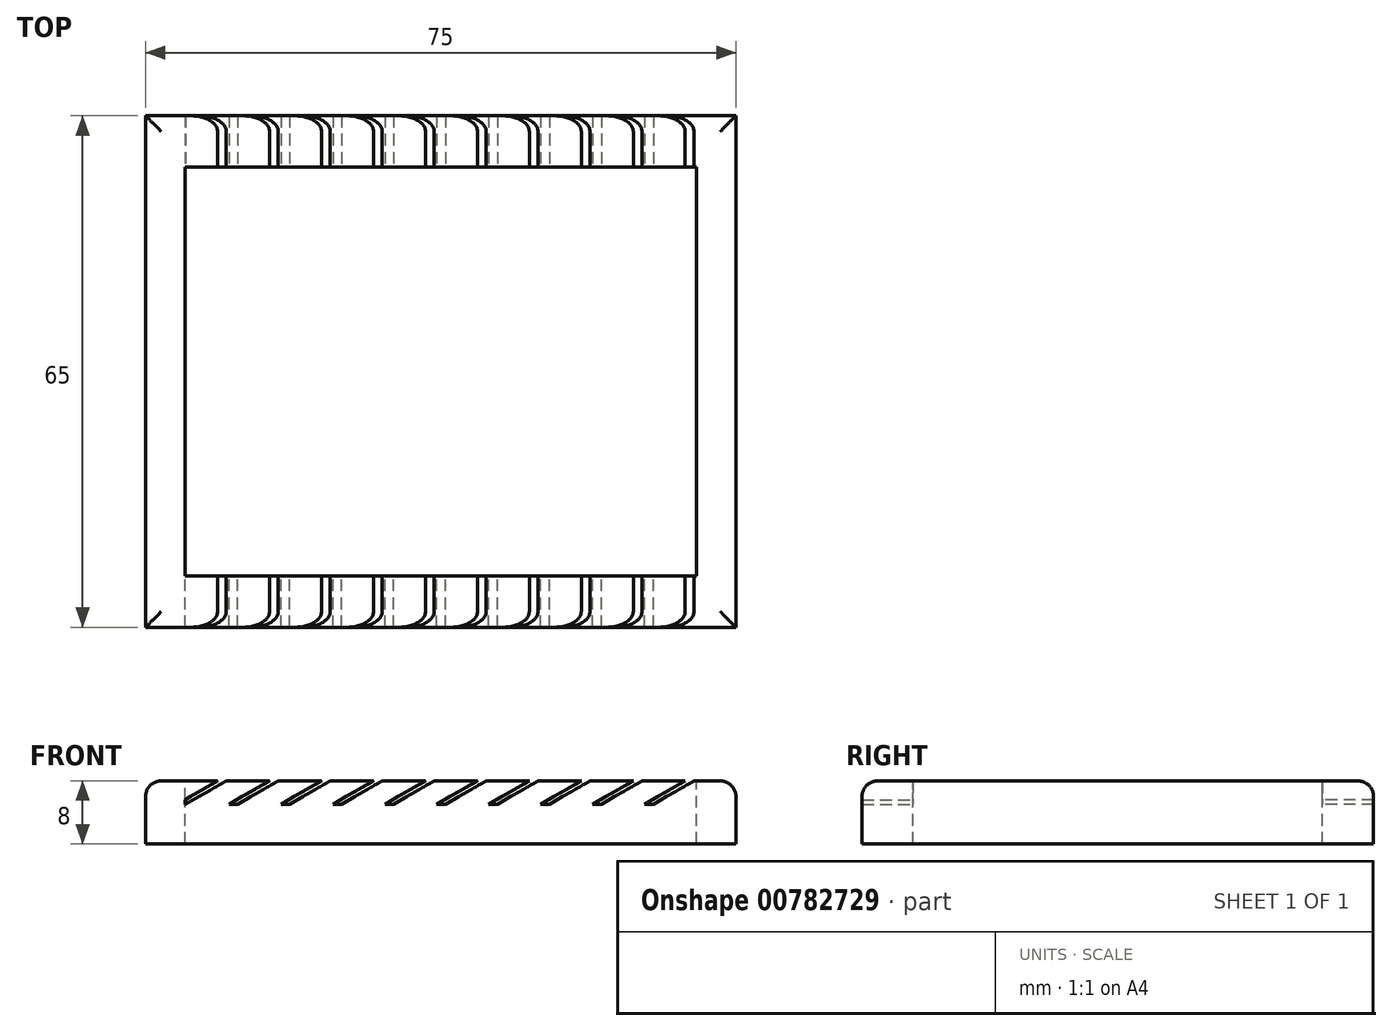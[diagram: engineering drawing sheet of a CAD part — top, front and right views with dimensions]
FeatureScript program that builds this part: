
annotation { "Feature Type Name" : "Feature", "Feature Type Description" : "" }
export const myFeature = defineFeature(function(context is Context, id is Id, definition is map)
    precondition{}
    {
        {
            var Q0;
            Q0=qCreatedBy(makeId("Top.planeOp"),FACE);
            var sketch = newSketch(context, id + "F0", { "sketchPlane" : qUnion([Q0])});
            skLineSegment(sketch, "E0.bottom", {"start": v(37.5, -32.5) * mm, "end": v(-37.5, -32.5) * mm});
            skLineSegment(sketch, "E0.top", {"start": v(37.5, 32.5) * mm, "end": v(-37.5, 32.5) * mm});
            skLineSegment(sketch, "E0.left", {"start": v(37.5, -32.5) * mm, "end": v(37.5, 32.5) * mm});
            skLineSegment(sketch, "E0.right", {"start": v(-37.5, -32.5) * mm, "end": v(-37.5, 32.5) * mm});
            skPoint(sketch, "E0.middle", {"position": v(0, 0) * mm});
            skSolve(sketch);
        }
        {
            var Q0;
            Q0=makeQuery(id+"F0.imprint","IMPRINT",FACE,{"disambiguationData":[TD([[makeQuery(id+"F0.imprint","IMPRINT",EDGE,{"derivedFrom":sQuery(id+"F0.wireOp",EDGE,"E0.bottom")}),-1.0]])]});
            extrude(context, id + "F1", {"entities" : qUnion([Q0]), "depth" : 8 * mm, "offsetDistance" : 25 * mm});
        }
        {
            var Q0;
            Q0=makeQuery(id+"F1.opExtrude","CAP_FACE",FACE,{"disambiguationData":[OSD([sQuery(id+"F0.wireOp",EDGE,"E0.bottom"),sQuery(id+"F0.wireOp",EDGE,"E0.top"),sQuery(id+"F0.wireOp",EDGE,"E0.left"),sQuery(id+"F0.wireOp",EDGE,"E0.right")])],"isStart":false});
            fillet(context, id + "F2", {"entities" : qUnion([Q0]), "radius" : 2 * mm, "tangentPropagation" : true, "allowEdgeOverflow" : false});
        }
        {
            var Q0;
            Q0=makeQuery(id+"F1.opExtrude","CAP_FACE",FACE,{"disambiguationData":[OSD([sQuery(id+"F0.wireOp",EDGE,"E0.bottom"),sQuery(id+"F0.wireOp",EDGE,"E0.top"),sQuery(id+"F0.wireOp",EDGE,"E0.left"),sQuery(id+"F0.wireOp",EDGE,"E0.right")])],"isStart":false});
            var sketch = newSketch(context, id + "F3", { "sketchPlane" : qUnion([Q0])});
            skLineSegment(sketch, "E1.bottom", {"start": v(32.5, -26) * mm, "end": v(-32.5, -26) * mm});
            skLineSegment(sketch, "E1.top", {"start": v(32.5, 26) * mm, "end": v(-32.5, 26) * mm});
            skLineSegment(sketch, "E1.left", {"start": v(32.5, -26) * mm, "end": v(32.5, 26) * mm});
            skLineSegment(sketch, "E1.right", {"start": v(-32.5, -26) * mm, "end": v(-32.5, 26) * mm});
            skPoint(sketch, "E1.middle", {"position": v(0, 0) * mm});
            skSolve(sketch);
        }
        {
            var Q0;
            Q0=makeQuery(id+"F3.imprint","IMPRINT",FACE,{"disambiguationData":[TD([[makeQuery(id+"F3.imprint","IMPRINT",EDGE,{"derivedFrom":sQuery(id+"F3.wireOp",EDGE,"E1.bottom")}),-1.0]])]});
            extrude(context, id + "F4", {"entities" : qUnion([Q0]), "operationType" : NewBodyOperationType.REMOVE, "endBound" : BoundingType.THROUGH_ALL, "oppositeDirection" : true, "depth" : 25 * mm, "offsetDistance" : 25 * mm});
        }
        {
            var Q0;
            Q0=makeQuery(id+"F4.boolean.opBoolean","COPY",FACE,{"derivedFrom":makeQuery(id+"F4.opExtrude","SWEPT_FACE",FACE,{"disambiguationData":[OSD([sQuery(id+"F3.wireOp",EDGE,"E1.top")])]})});
            var sketch = newSketch(context, id + "F5", { "sketchPlane" : qUnion([Q0])});
            skLineSegment(sketch, "E2", {"start": v(-28.34, 8) * mm, "end": v(-27.24, 8) * mm});
            skLineSegment(sketch, "E3", {"start": v(-27.24, 8) * mm, "end": v(-32.4, 5.02) * mm});
            skLineSegment(sketch, "E4", {"start": v(-32.4, 5.02) * mm, "end": v(-33.5, 5.02) * mm});
            skLineSegment(sketch, "E5", {"start": v(-33.5, 5.02) * mm, "end": v(-28.34, 8) * mm});
            skLineSegment(sketch, "E6.1.0.0", {"start": v(-20.64, 8) * mm, "end": v(-25.8, 5.02) * mm});
            skLineSegment(sketch, "E6.1.0.1", {"start": v(-26.9, 5.02) * mm, "end": v(-21.74, 8) * mm});
            skLineSegment(sketch, "E6.1.0.2", {"start": v(-21.74, 8) * mm, "end": v(-20.64, 8) * mm});
            skLineSegment(sketch, "E6.1.0.3", {"start": v(-25.8, 5.02) * mm, "end": v(-26.9, 5.02) * mm});
            skLineSegment(sketch, "E6.2.0.0", {"start": v(-14.04, 8) * mm, "end": v(-19.2, 5.02) * mm});
            skLineSegment(sketch, "E6.2.0.1", {"start": v(-20.3, 5.02) * mm, "end": v(-15.14, 8) * mm});
            skLineSegment(sketch, "E6.2.0.2", {"start": v(-15.14, 8) * mm, "end": v(-14.04, 8) * mm});
            skLineSegment(sketch, "E6.2.0.3", {"start": v(-19.2, 5.02) * mm, "end": v(-20.3, 5.02) * mm});
            skLineSegment(sketch, "E6.3.0.0", {"start": v(-7.44, 8) * mm, "end": v(-12.6, 5.02) * mm});
            skLineSegment(sketch, "E6.3.0.1", {"start": v(-13.7, 5.02) * mm, "end": v(-8.54, 8) * mm});
            skLineSegment(sketch, "E6.3.0.2", {"start": v(-8.54, 8) * mm, "end": v(-7.44, 8) * mm});
            skLineSegment(sketch, "E6.3.0.3", {"start": v(-12.6, 5.02) * mm, "end": v(-13.7, 5.02) * mm});
            skLineSegment(sketch, "E6.4.0.0", {"start": v(-0.84, 8) * mm, "end": v(-6, 5.02) * mm});
            skLineSegment(sketch, "E6.4.0.1", {"start": v(-7.1, 5.02) * mm, "end": v(-1.94, 8) * mm});
            skLineSegment(sketch, "E6.4.0.2", {"start": v(-1.94, 8) * mm, "end": v(-0.84, 8) * mm});
            skLineSegment(sketch, "E6.4.0.3", {"start": v(-6, 5.02) * mm, "end": v(-7.1, 5.02) * mm});
            skLineSegment(sketch, "E6.5.0.0", {"start": v(5.76, 8) * mm, "end": v(0.6, 5.02) * mm});
            skLineSegment(sketch, "E6.5.0.1", {"start": v(-0.5, 5.02) * mm, "end": v(4.66, 8) * mm});
            skLineSegment(sketch, "E6.5.0.2", {"start": v(4.66, 8) * mm, "end": v(5.76, 8) * mm});
            skLineSegment(sketch, "E6.5.0.3", {"start": v(0.6, 5.02) * mm, "end": v(-0.5, 5.02) * mm});
            skLineSegment(sketch, "E6.6.0.0", {"start": v(12.36, 8) * mm, "end": v(7.2, 5.02) * mm});
            skLineSegment(sketch, "E6.6.0.1", {"start": v(6.1, 5.02) * mm, "end": v(11.26, 8) * mm});
            skLineSegment(sketch, "E6.6.0.2", {"start": v(11.26, 8) * mm, "end": v(12.36, 8) * mm});
            skLineSegment(sketch, "E6.6.0.3", {"start": v(7.2, 5.02) * mm, "end": v(6.1, 5.02) * mm});
            skLineSegment(sketch, "E6.7.0.0", {"start": v(18.96, 8) * mm, "end": v(13.8, 5.02) * mm});
            skLineSegment(sketch, "E6.7.0.1", {"start": v(12.7, 5.02) * mm, "end": v(17.86, 8) * mm});
            skLineSegment(sketch, "E6.7.0.2", {"start": v(17.86, 8) * mm, "end": v(18.96, 8) * mm});
            skLineSegment(sketch, "E6.7.0.3", {"start": v(13.8, 5.02) * mm, "end": v(12.7, 5.02) * mm});
            skLineSegment(sketch, "E6.8.0.0", {"start": v(25.56, 8) * mm, "end": v(20.4, 5.02) * mm});
            skLineSegment(sketch, "E6.8.0.1", {"start": v(19.3, 5.02) * mm, "end": v(24.46, 8) * mm});
            skLineSegment(sketch, "E6.8.0.2", {"start": v(24.46, 8) * mm, "end": v(25.56, 8) * mm});
            skLineSegment(sketch, "E6.8.0.3", {"start": v(20.4, 5.02) * mm, "end": v(19.3, 5.02) * mm});
            skLineSegment(sketch, "E6.9.0.0", {"start": v(32.16, 8) * mm, "end": v(27, 5.02) * mm});
            skLineSegment(sketch, "E6.9.0.1", {"start": v(25.9, 5.02) * mm, "end": v(31.06, 8) * mm});
            skLineSegment(sketch, "E6.9.0.2", {"start": v(31.06, 8) * mm, "end": v(32.16, 8) * mm});
            skLineSegment(sketch, "E6.9.0.3", {"start": v(27, 5.02) * mm, "end": v(25.9, 5.02) * mm});
            skLineSegment(sketch, "E6.direction1", {"start": v(-32.4, 5.02) * mm, "end": v(-25.8, 5.02) * mm, "construction": true});
            skSolve(sketch);
        }
        {
            var Q0;
            Q0=makeQuery(id+"F4.boolean.opBoolean","COPY",FACE,{"derivedFrom":makeQuery(id+"F4.opExtrude","SWEPT_FACE",FACE,{"disambiguationData":[OSD([sQuery(id+"F3.wireOp",EDGE,"E1.bottom")])]})});
            var sketch = newSketch(context, id + "F6", { "sketchPlane" : qUnion([Q0])});
            skLineSegment(sketch, "E7.0.0", {"start": v(28.34, 8) * mm, "end": v(32.5, 5.6) * mm});
            skLineSegment(sketch, "E7.0.1", {"start": v(32.5, 5.6) * mm, "end": v(32.45, 5) * mm});
            skLineSegment(sketch, "E7.0.2", {"start": v(32.45, 5) * mm, "end": v(27.24, 8) * mm});
            skLineSegment(sketch, "E7.0.3", {"start": v(27.24, 8) * mm, "end": v(28.34, 8) * mm});
            skLineSegment(sketch, "E8.0.0", {"start": v(21.74, 8) * mm, "end": v(26.9, 5.02) * mm});
            skLineSegment(sketch, "E8.0.1", {"start": v(26.9, 5.02) * mm, "end": v(25.8, 5.02) * mm});
            skLineSegment(sketch, "E8.0.2", {"start": v(25.8, 5.02) * mm, "end": v(20.64, 8) * mm});
            skLineSegment(sketch, "E8.0.3", {"start": v(20.64, 8) * mm, "end": v(21.74, 8) * mm});
            skLineSegment(sketch, "E9.0.0", {"start": v(15.14, 8) * mm, "end": v(20.3, 5.02) * mm});
            skLineSegment(sketch, "E9.0.1", {"start": v(20.3, 5.02) * mm, "end": v(19.2, 5.02) * mm});
            skLineSegment(sketch, "E9.0.2", {"start": v(19.2, 5.02) * mm, "end": v(14.04, 8) * mm});
            skLineSegment(sketch, "E9.0.3", {"start": v(14.04, 8) * mm, "end": v(15.14, 8) * mm});
            skLineSegment(sketch, "E10.0.0", {"start": v(8.54, 8) * mm, "end": v(13.7, 5.02) * mm});
            skLineSegment(sketch, "E10.0.1", {"start": v(13.7, 5.02) * mm, "end": v(12.6, 5.02) * mm});
            skLineSegment(sketch, "E10.0.2", {"start": v(12.6, 5.02) * mm, "end": v(7.44, 8) * mm});
            skLineSegment(sketch, "E10.0.3", {"start": v(7.44, 8) * mm, "end": v(8.54, 8) * mm});
            skLineSegment(sketch, "E11.0.0", {"start": v(1.94, 8) * mm, "end": v(7.1, 5.02) * mm});
            skLineSegment(sketch, "E11.0.1", {"start": v(7.1, 5.02) * mm, "end": v(6, 5.02) * mm});
            skLineSegment(sketch, "E11.0.2", {"start": v(6, 5.02) * mm, "end": v(0.84, 8) * mm});
            skLineSegment(sketch, "E11.0.3", {"start": v(0.84, 8) * mm, "end": v(1.94, 8) * mm});
            skPoint(sketch, "E12.0", {"position": v(-3.18, 6.51) * mm});
            skLineSegment(sketch, "E13.0.0", {"start": v(-4.66, 8) * mm, "end": v(0.5, 5.02) * mm});
            skLineSegment(sketch, "E13.0.1", {"start": v(0.5, 5.02) * mm, "end": v(-0.6, 5.02) * mm});
            skLineSegment(sketch, "E13.0.2", {"start": v(-0.6, 5.02) * mm, "end": v(-5.76, 8) * mm});
            skLineSegment(sketch, "E13.0.3", {"start": v(-5.76, 8) * mm, "end": v(-4.66, 8) * mm});
            skLineSegment(sketch, "E14.0.0", {"start": v(-11.26, 8) * mm, "end": v(-6.1, 5.02) * mm});
            skLineSegment(sketch, "E14.0.1", {"start": v(-6.1, 5.02) * mm, "end": v(-7.2, 5.02) * mm});
            skLineSegment(sketch, "E14.0.2", {"start": v(-7.2, 5.02) * mm, "end": v(-12.36, 8) * mm});
            skLineSegment(sketch, "E14.0.3", {"start": v(-12.36, 8) * mm, "end": v(-11.26, 8) * mm});
            skLineSegment(sketch, "E15.0.0", {"start": v(-17.86, 8) * mm, "end": v(-12.7, 5.02) * mm});
            skLineSegment(sketch, "E15.0.1", {"start": v(-12.7, 5.02) * mm, "end": v(-13.8, 5.02) * mm});
            skLineSegment(sketch, "E15.0.2", {"start": v(-13.8, 5.02) * mm, "end": v(-18.96, 8) * mm});
            skLineSegment(sketch, "E15.0.3", {"start": v(-18.96, 8) * mm, "end": v(-17.86, 8) * mm});
            skLineSegment(sketch, "E16.0.0", {"start": v(-24.46, 8) * mm, "end": v(-19.3, 5.02) * mm});
            skLineSegment(sketch, "E16.0.1", {"start": v(-19.3, 5.02) * mm, "end": v(-20.4, 5.02) * mm});
            skLineSegment(sketch, "E16.0.2", {"start": v(-20.4, 5.02) * mm, "end": v(-25.56, 8) * mm});
            skLineSegment(sketch, "E16.0.3", {"start": v(-25.56, 8) * mm, "end": v(-24.46, 8) * mm});
            skLineSegment(sketch, "E17.0.0", {"start": v(-31.06, 8) * mm, "end": v(-25.9, 5.02) * mm});
            skLineSegment(sketch, "E17.0.1", {"start": v(-25.9, 5.02) * mm, "end": v(-27, 5.02) * mm});
            skLineSegment(sketch, "E17.0.2", {"start": v(-27, 5.02) * mm, "end": v(-32.16, 8) * mm});
            skLineSegment(sketch, "E17.0.3", {"start": v(-32.16, 8) * mm, "end": v(-31.06, 8) * mm});
            skSolve(sketch);
        }
        {
            var Q0;
            {var subQ0=sQuery(id+"F5.wireOp",EDGE,"E2");Q0=makeQuery(id+"F5.imprint","IMPRINT",FACE,{"disambiguationData":[TD([[makeQuery(id+"F5.imprint","IMPRINT",EDGE,{"derivedFrom":subQ0}),1.0]])]});}
            var Q1;
            Q1=makeQuery(id+"F5.imprint","IMPRINT",FACE,{"disambiguationData":[TD([[makeQuery(id+"F5.imprint","IMPRINT",EDGE,{"derivedFrom":sQuery(id+"F5.wireOp",EDGE,"E6.1.0.0")}),-1.0]])]});
            var Q2;
            Q2=makeQuery(id+"F5.imprint","IMPRINT",FACE,{"disambiguationData":[TD([[makeQuery(id+"F5.imprint","IMPRINT",EDGE,{"derivedFrom":sQuery(id+"F5.wireOp",EDGE,"E6.2.0.0")}),-1.0]])]});
            var Q3;
            Q3=makeQuery(id+"F5.imprint","IMPRINT",FACE,{"disambiguationData":[TD([[makeQuery(id+"F5.imprint","IMPRINT",EDGE,{"derivedFrom":sQuery(id+"F5.wireOp",EDGE,"E6.3.0.0")}),-1.0]])]});
            var Q4;
            Q4=makeQuery(id+"F5.imprint","IMPRINT",FACE,{"disambiguationData":[TD([[makeQuery(id+"F5.imprint","IMPRINT",EDGE,{"derivedFrom":sQuery(id+"F5.wireOp",EDGE,"E6.4.0.0")}),-1.0]])]});
            var Q5;
            Q5=makeQuery(id+"F5.imprint","IMPRINT",FACE,{"disambiguationData":[TD([[makeQuery(id+"F5.imprint","IMPRINT",EDGE,{"derivedFrom":sQuery(id+"F5.wireOp",EDGE,"E6.5.0.0")}),-1.0]])]});
            var Q6;
            Q6=makeQuery(id+"F5.imprint","IMPRINT",FACE,{"disambiguationData":[TD([[makeQuery(id+"F5.imprint","IMPRINT",EDGE,{"derivedFrom":sQuery(id+"F5.wireOp",EDGE,"E6.6.0.0")}),-1.0]])]});
            var Q7;
            Q7=makeQuery(id+"F5.imprint","IMPRINT",FACE,{"disambiguationData":[TD([[makeQuery(id+"F5.imprint","IMPRINT",EDGE,{"derivedFrom":sQuery(id+"F5.wireOp",EDGE,"E6.7.0.0")}),-1.0]])]});
            var Q8;
            Q8=makeQuery(id+"F5.imprint","IMPRINT",FACE,{"disambiguationData":[TD([[makeQuery(id+"F5.imprint","IMPRINT",EDGE,{"derivedFrom":sQuery(id+"F5.wireOp",EDGE,"E6.8.0.0")}),-1.0]])]});
            var Q9;
            Q9=makeQuery(id+"F5.imprint","IMPRINT",FACE,{"disambiguationData":[TD([[makeQuery(id+"F5.imprint","IMPRINT",EDGE,{"derivedFrom":sQuery(id+"F5.wireOp",EDGE,"E6.9.0.0")}),-1.0]])]});
            extrude(context, id + "F7", {"entities" : qUnion([Q0, Q1, Q2, Q3, Q4, Q5, Q6, Q7, Q8, Q9]), "operationType" : NewBodyOperationType.REMOVE, "endBound" : BoundingType.THROUGH_ALL, "oppositeDirection" : true, "depth" : 25 * mm, "offsetDistance" : 25 * mm});
        }
        {
            var Q0;
            Q0=makeQuery(id+"F6.imprint","IMPRINT",FACE,{"disambiguationData":[TD([[makeQuery(id+"F6.imprint","IMPRINT",EDGE,{"derivedFrom":sQuery(id+"F6.wireOp",EDGE,"E7.0.0")}),-1.0]])]});
            var Q1;
            Q1=makeQuery(id+"F6.imprint","IMPRINT",FACE,{"disambiguationData":[TD([[makeQuery(id+"F6.imprint","IMPRINT",EDGE,{"derivedFrom":sQuery(id+"F6.wireOp",EDGE,"E8.0.0")}),-1.0]])]});
            var Q2;
            Q2=makeQuery(id+"F6.imprint","IMPRINT",FACE,{"disambiguationData":[TD([[makeQuery(id+"F6.imprint","IMPRINT",EDGE,{"derivedFrom":sQuery(id+"F6.wireOp",EDGE,"E9.0.0")}),-1.0]])]});
            var Q3;
            Q3=makeQuery(id+"F6.imprint","IMPRINT",FACE,{"disambiguationData":[TD([[makeQuery(id+"F6.imprint","IMPRINT",EDGE,{"derivedFrom":sQuery(id+"F6.wireOp",EDGE,"E10.0.0")}),-1.0]])]});
            var Q4;
            Q4=makeQuery(id+"F6.imprint","IMPRINT",FACE,{"disambiguationData":[TD([[makeQuery(id+"F6.imprint","IMPRINT",EDGE,{"derivedFrom":sQuery(id+"F6.wireOp",EDGE,"E11.0.0")}),-1.0]])]});
            var Q5;
            Q5=makeQuery(id+"F6.imprint","IMPRINT",FACE,{"disambiguationData":[TD([[makeQuery(id+"F6.imprint","IMPRINT",EDGE,{"derivedFrom":sQuery(id+"F6.wireOp",EDGE,"E13.0.0")}),-1.0]])]});
            var Q6;
            Q6=makeQuery(id+"F6.imprint","IMPRINT",FACE,{"disambiguationData":[TD([[makeQuery(id+"F6.imprint","IMPRINT",EDGE,{"derivedFrom":sQuery(id+"F6.wireOp",EDGE,"E14.0.0")}),-1.0]])]});
            var Q7;
            Q7=makeQuery(id+"F6.imprint","IMPRINT",FACE,{"disambiguationData":[TD([[makeQuery(id+"F6.imprint","IMPRINT",EDGE,{"derivedFrom":sQuery(id+"F6.wireOp",EDGE,"E15.0.0")}),-1.0]])]});
            var Q8;
            Q8=makeQuery(id+"F6.imprint","IMPRINT",FACE,{"disambiguationData":[TD([[makeQuery(id+"F6.imprint","IMPRINT",EDGE,{"derivedFrom":sQuery(id+"F6.wireOp",EDGE,"E16.0.0")}),-1.0]])]});
            var Q9;
            Q9=makeQuery(id+"F6.imprint","IMPRINT",FACE,{"disambiguationData":[TD([[makeQuery(id+"F6.imprint","IMPRINT",EDGE,{"derivedFrom":sQuery(id+"F6.wireOp",EDGE,"E17.0.0")}),-1.0]])]});
            extrude(context, id + "F8", {"entities" : qUnion([Q0, Q1, Q2, Q3, Q4, Q5, Q6, Q7, Q8, Q9]), "operationType" : NewBodyOperationType.REMOVE, "endBound" : BoundingType.THROUGH_ALL, "oppositeDirection" : true, "depth" : 25 * mm, "offsetDistance" : 25 * mm});
        }
    });
